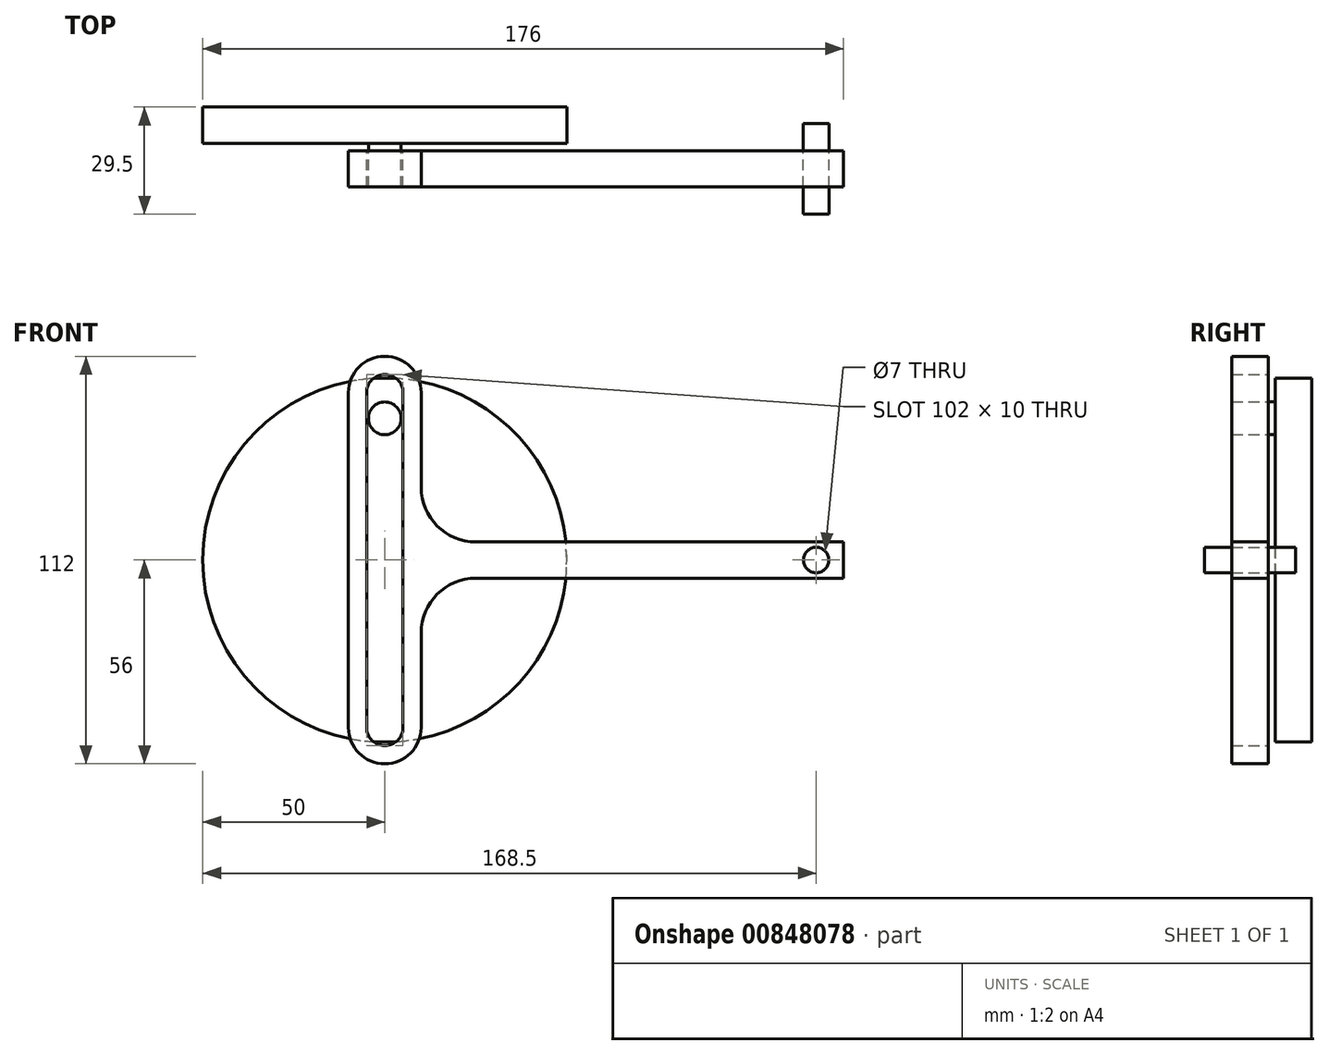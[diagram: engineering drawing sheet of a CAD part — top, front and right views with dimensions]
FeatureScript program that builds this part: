
annotation { "Feature Type Name" : "Feature", "Feature Type Description" : "" }
export const myFeature = defineFeature(function(context is Context, id is Id, definition is map)
    precondition{}
    {
        {
            var Q0;
            Q0=qCreatedBy(makeId("Front.planeOp"),FACE);
            var sketch = newSketch(context, id + "F0", { "sketchPlane" : qUnion([Q0])});
            skLineSegment(sketch, "E0.bottom", {"start": v(-5, 51) * mm, "end": v(-5, 51) * mm});
            skLineSegment(sketch, "E0.top", {"start": v(-5, -51) * mm, "end": v(-5, -51) * mm});
            skLineSegment(sketch, "E0.left", {"start": v(0, 46) * mm, "end": v(0, -46) * mm});
            skLineSegment(sketch, "E0.right", {"start": v(-10, 46) * mm, "end": v(-10, -46) * mm});
            skPoint(sketch, "E1.visualSharp", {"position": v(-10, 51) * mm});
            skArc(sketch, "E1.filletArc", {"start": v(-5, 51) * mm, "mid": v(-8.54, 49.54) * mm, "end": v(-10, 46) * mm});
            skPoint(sketch, "E2.visualSharp", {"position": v(0, 51) * mm});
            skArc(sketch, "E2.filletArc", {"start": v(0, 46) * mm, "mid": v(-1.46, 49.54) * mm, "end": v(-5, 51) * mm});
            skPoint(sketch, "E3.visualSharp", {"position": v(0, -51) * mm});
            skArc(sketch, "E3.filletArc", {"start": v(-5, -51) * mm, "mid": v(-1.46, -49.54) * mm, "end": v(0, -46) * mm});
            skPoint(sketch, "E4.visualSharp", {"position": v(-10, -51) * mm});
            skArc(sketch, "E4.filletArc", {"start": v(-10, -46) * mm, "mid": v(-8.54, -49.54) * mm, "end": v(-5, -51) * mm});
            skArc(sketch, "E5.0", {"start": v(-5, 56) * mm, "mid": v(-12.07, 53.07) * mm, "end": v(-15, 46) * mm});
            skArc(sketch, "E5.1", {"start": v(-15, -46) * mm, "mid": v(-12.07, -53.07) * mm, "end": v(-5, -56) * mm});
            skArc(sketch, "E5.2", {"start": v(-5, -56) * mm, "mid": v(2.07, -53.07) * mm, "end": v(5, -46) * mm});
            skLineSegment(sketch, "E5.3", {"start": v(-15, 46) * mm, "end": v(-15, -46) * mm});
            skLineSegment(sketch, "E5.4", {"start": v(5, 46) * mm, "end": v(5, -46) * mm});
            skArc(sketch, "E5.5", {"start": v(5, 46) * mm, "mid": v(2.07, 53.07) * mm, "end": v(-5, 56) * mm});
            skLineSegment(sketch, "E6", {"start": v(5, 5) * mm, "end": v(121, 5) * mm});
            skLineSegment(sketch, "E7", {"start": v(121, 5) * mm, "end": v(121, -5) * mm});
            skLineSegment(sketch, "E8", {"start": v(121, -5) * mm, "end": v(5, -5) * mm});
            skPoint(sketch, "E9", {"position": v(5, 0) * mm});
            skCircle(sketch, "E10", {"center": v(113.5, 0) * mm, "radius": 3.5 * mm});
            skPoint(sketch, "E11", {"position": v(121, 0) * mm});
            skSolve(sketch);
        }
        {
            var Q0;
            Q0=makeQuery(id+"F0.imprint","IMPRINT",FACE,{"disambiguationData":[TD([[makeQuery(id+"F0.imprint","IMPRINT",EDGE,{"derivedFrom":sQuery(id+"F0.wireOp",EDGE,"E0.left")}),1.0]])]});
            var Q1;
            {var subQ0=sQuery(id+"F0.wireOp",EDGE,"E6");Q1=makeQuery(id+"F0.imprint","IMPRINT",FACE,{"disambiguationData":[TD([[makeQuery(id+"F0.imprint","IMPRINT",EDGE,{"derivedFrom":subQ0}),-1.0]])]});}
            extrude(context, id + "F1", {"entities" : qUnion([Q0, Q1]), "endBound" : BoundingType.SYMMETRIC, "depth" : 10 * mm, "offsetDistance" : 25 * mm});
        }
        {
            var Q0;
            Q0=makeQuery(id+"F1.opExtrude","CAP_FACE",FACE,{"disambiguationData":[OSD([sQuery(id+"F0.wireOp",EDGE,"E0.left"),sQuery(id+"F0.wireOp",EDGE,"E0.right"),sQuery(id+"F0.wireOp",EDGE,"E1.filletArc"),sQuery(id+"F0.wireOp",EDGE,"E2.filletArc"),sQuery(id+"F0.wireOp",EDGE,"E3.filletArc"),sQuery(id+"F0.wireOp",EDGE,"E4.filletArc"),sQuery(id+"F0.wireOp",EDGE,"E5.0"),sQuery(id+"F0.wireOp",EDGE,"E5.1"),sQuery(id+"F0.wireOp",EDGE,"E5.2"),sQuery(id+"F0.wireOp",EDGE,"E5.3"),sQuery(id+"F0.wireOp",EDGE,"E5.4"),sQuery(id+"F0.wireOp",EDGE,"E5.5"),sQuery(id+"F0.wireOp",EDGE,"E6"),sQuery(id+"F0.wireOp",EDGE,"E7"),sQuery(id+"F0.wireOp",EDGE,"E8"),sQuery(id+"F0.wireOp",EDGE,"E10")])],"isStart":true});
            cPlane(context, id + "F2", {"entities" : qUnion([Q0]), "cplaneType" : CPlaneType.OFFSET, "offset" : 12 * mm, "width" : 150 * mm, "height" : 150 * mm});
        }
        {
            var Q0;
            Q0=qCreatedBy(id+"F2.planeOp",FACE);
            var sketch = newSketch(context, id + "F3", { "sketchPlane" : qUnion([Q0])});
            skCircle(sketch, "E12", {"center": v(5, 38.94) * mm, "radius": 4.5 * mm});
            skPoint(sketch, "E13.0", {"position": v(5, 51) * mm});
            skCircle(sketch, "E14", {"center": v(5, 0) * mm, "radius": 50 * mm});
            skPoint(sketch, "E15.0", {"position": v(5, -51) * mm});
            skSolve(sketch);
        }
        {
            var Q0;
            Q0=makeQuery(id+"F3.imprint","IMPRINT",FACE,{"disambiguationData":[TD([[makeQuery(id+"F3.imprint","IMPRINT",EDGE,{"derivedFrom":sQuery(id+"F3.wireOp",EDGE,"E12")}),-1.0]])]});
            var Q1;
            Q1=makeQuery(id+"F3.imprint","IMPRINT",FACE,{"disambiguationData":[TD([[makeQuery(id+"F3.imprint","IMPRINT",EDGE,{"derivedFrom":sQuery(id+"F3.wireOp",EDGE,"E12")}),1.0]])]});
            extrude(context, id + "F4", {"entities" : qUnion([Q0, Q1]), "oppositeDirection" : true, "depth" : 10 * mm, "offsetDistance" : 25 * mm});
        }
        {
            var Q0;
            Q0=makeQuery(id+"F3.imprint","IMPRINT",FACE,{"disambiguationData":[TD([[makeQuery(id+"F3.imprint","IMPRINT",EDGE,{"derivedFrom":sQuery(id+"F3.wireOp",EDGE,"E12")}),1.0]])]});
            var Q1;
            Q1=makeQuery(id+"F1.opExtrude","CAP_FACE",FACE,{"disambiguationData":[OSD([sQuery(id+"F0.wireOp",EDGE,"E0.left"),sQuery(id+"F0.wireOp",EDGE,"E0.right"),sQuery(id+"F0.wireOp",EDGE,"E1.filletArc"),sQuery(id+"F0.wireOp",EDGE,"E2.filletArc"),sQuery(id+"F0.wireOp",EDGE,"E3.filletArc"),sQuery(id+"F0.wireOp",EDGE,"E4.filletArc"),sQuery(id+"F0.wireOp",EDGE,"E5.0"),sQuery(id+"F0.wireOp",EDGE,"E5.1"),sQuery(id+"F0.wireOp",EDGE,"E5.2"),sQuery(id+"F0.wireOp",EDGE,"E5.3"),sQuery(id+"F0.wireOp",EDGE,"E5.4"),sQuery(id+"F0.wireOp",EDGE,"E5.5"),sQuery(id+"F0.wireOp",EDGE,"E6"),sQuery(id+"F0.wireOp",EDGE,"E7"),sQuery(id+"F0.wireOp",EDGE,"E8"),sQuery(id+"F0.wireOp",EDGE,"E10")])],"isStart":false});
            extrude(context, id + "F5", {"entities" : qUnion([Q0]), "operationType" : NewBodyOperationType.ADD, "endBound" : BoundingType.UP_TO_SURFACE, "oppositeDirection" : true, "depth" : 25 * mm, "endBoundEntityFace" : qUnion([Q1]), "offsetDistance" : 25 * mm});
        }
        {
            var Q0;
            Q0=makeQuery(id+"F1.opExtrude","SWEPT_EDGE",EDGE,{"disambiguationData":[OSD([sQuery(id+"F0.wireOp",EDGE,"E5.4"),sQuery(id+"F0.wireOp",EDGE,"E6")])]});
            var Q1;
            Q1=makeQuery(id+"F1.opExtrude","SWEPT_EDGE",EDGE,{"disambiguationData":[OSD([sQuery(id+"F0.wireOp",EDGE,"E5.4"),sQuery(id+"F0.wireOp",EDGE,"E8")])]});
            fillet(context, id + "F6", {"entities" : qUnion([Q0, Q1]), "radius" : 15 * mm, "tangentPropagation" : true, "allowEdgeOverflow" : false});
        }
        {
            var Q0;
            Q0=makeQuery(id+"F0.imprint","IMPRINT",FACE,{"disambiguationData":[TD([[makeQuery(id+"F0.imprint","IMPRINT",EDGE,{"derivedFrom":sQuery(id+"F0.wireOp",EDGE,"E10")}),1.0]])]});
            extrude(context, id + "F7", {"entities" : qUnion([Q0]), "endBound" : BoundingType.SYMMETRIC, "depth" : 25 * mm, "offsetDistance" : 25 * mm});
        }
    });
